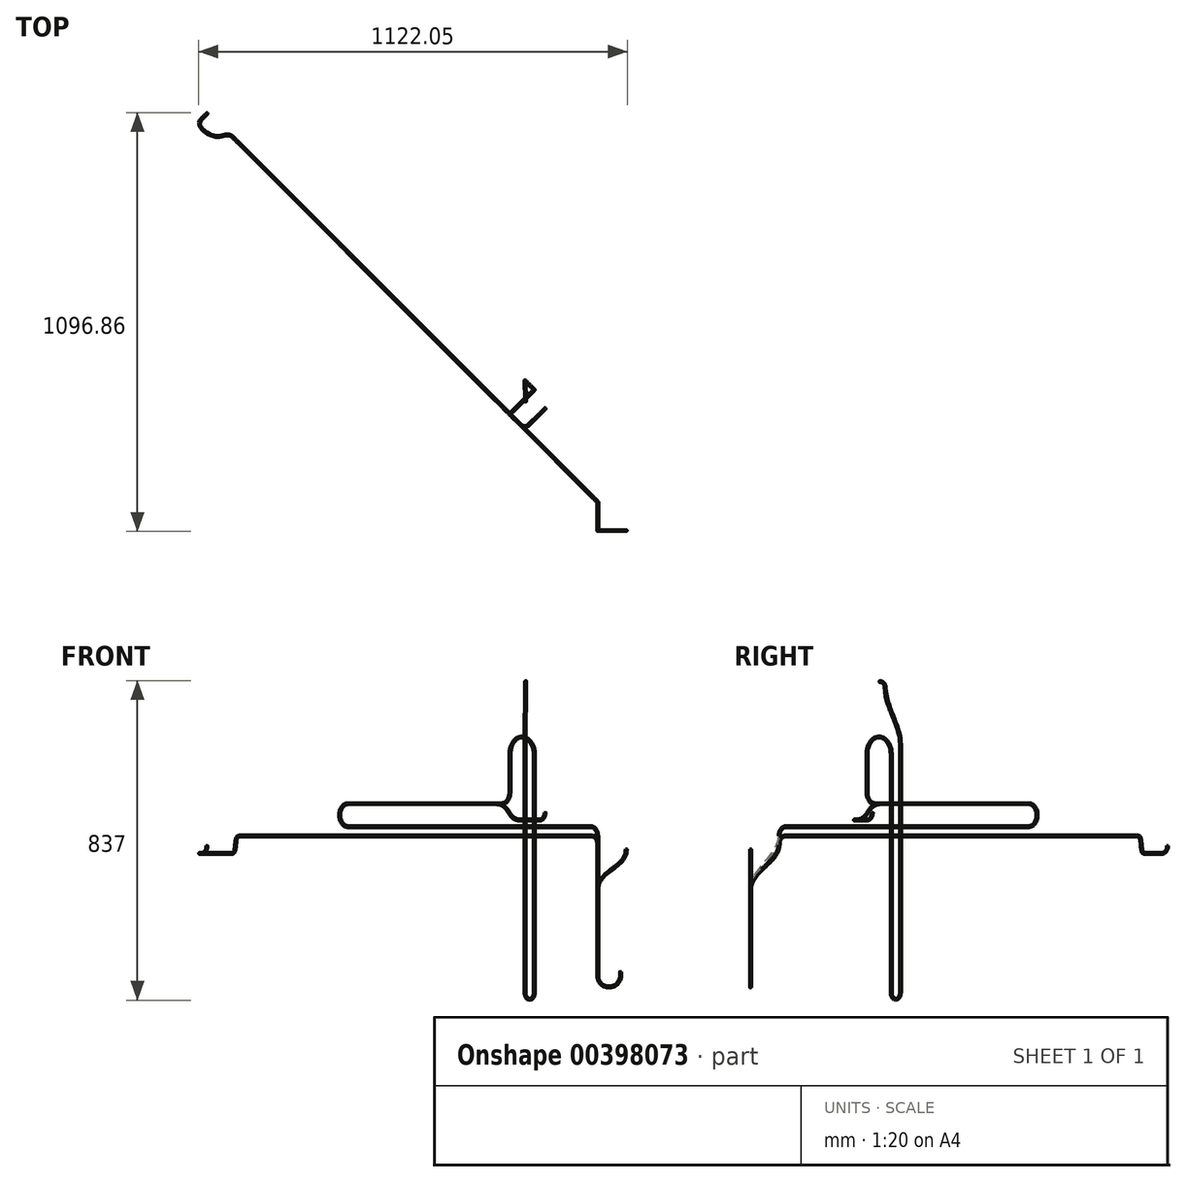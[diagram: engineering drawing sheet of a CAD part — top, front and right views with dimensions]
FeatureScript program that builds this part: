
annotation { "Feature Type Name" : "Feature", "Feature Type Description" : "" }
export const myFeature = defineFeature(function(context is Context, id is Id, definition is map)
    precondition{}
    {
        {
            var Q0;
            Q0=qCreatedBy(makeId("Top.planeOp"),FACE);
            var sketch = newSketch(context, id + "F0", { "sketchPlane" : qUnion([Q0])});
            skCircle(sketch, "E0", {"center": v(0, 0) * mm, "radius": 2.5 * mm});
            skSolve(sketch);
        }
        {
            var Q0;
            Q0=qCreatedBy(makeId("Front.planeOp"),FACE);
            var sketch = newSketch(context, id + "F1", { "sketchPlane" : qUnion([Q0])});
            skLineSegment(sketch, "E1", {"start": v(0, 0) * mm, "end": v(0, -10) * mm});
            skArc(sketch, "E2", {"start": v(-60, -10) * mm, "mid": v(-30, -40) * mm, "end": v(0, -10) * mm});
            skLineSegment(sketch, "E3", {"start": v(-60, -10) * mm, "end": v(-60, 215) * mm});
            skFitSpline(sketch, "E4", {"points": [v(-60, 215) * mm, v(-22.5, 268) * mm, v(15, 321) * mm], "startDerivative": vector(0, 150) * mm, "endDerivative": vector(0, 150) * mm});
            skLineSegment(sketch, "E5", {"start": v(15, 296) * mm, "end": v(15, 321) * mm, "construction": true});
            skLineSegment(sketch, "E6", {"start": v(-60, 240) * mm, "end": v(-60, 215) * mm, "construction": true});
            skLineSegment(sketch, "E7", {"start": v(15, 321) * mm, "end": v(-60, 215) * mm, "construction": true});
            skSolve(sketch);
        }
        {
            var Q0;
            Q0=qSketchRegion(id+"F0",true);
            var Q1;
            Q1=qConstructionFilter(qBodyType(qCreatedBy(id+"F1",EDGE),BodyType.WIRE),ConstructionObject.NO);
            sweep(context, id + "F2", {"profiles" : qUnion([Q0]), "path" : qUnion([Q1])});
        }
        {
            var Q0;
            Q0=qCreatedBy(makeId("Front.planeOp"),FACE);
            var sketch = newSketch(context, id + "F3", { "sketchPlane" : qUnion([Q0])});
            skLineSegment(sketch, "E8", {"start": v(0, 0) * mm, "end": v(0, -10) * mm});
            skArc(sketch, "E9", {"start": v(-60, -10) * mm, "mid": v(-30, -40) * mm, "end": v(0, -10) * mm});
            skLineSegment(sketch, "E10", {"start": v(-60, -10) * mm, "end": v(-60, 215) * mm});
            skSolve(sketch);
        }
        {
            var Q0;
            Q0=qCreatedBy(makeId("Right.planeOp"),FACE);
            var Q1;
            Q1=sQuery(id+"F3.wireOp",VERTEX,"E10.end");
            cPlane(context, id + "F4", {"entities" : qUnion([Q0, Q1]), "cplaneType" : CPlaneType.PLANE_POINT, "offset" : 25 * mm, "width" : 150 * mm, "height" : 150 * mm});
        }
        {
            var Q0;
            Q0=qCreatedBy(id+"F4.planeOp",FACE);
            var sketch = newSketch(context, id + "F5", { "sketchPlane" : qUnion([Q0])});
            skFitSpline(sketch, "E11", {"points": [v(0, 215) * mm, v(37.5, 275) * mm, v(75, 335) * mm], "startDerivative": vector(0, 150) * mm, "endDerivative": vector(0, 150) * mm});
            skLineSegment(sketch, "E12", {"start": v(75, 310) * mm, "end": v(75, 335) * mm, "construction": true});
            skLineSegment(sketch, "E13", {"start": v(0, 240) * mm, "end": v(0, 215) * mm, "construction": true});
            skLineSegment(sketch, "E14", {"start": v(0, 215) * mm, "end": v(75, 335) * mm, "construction": true});
            skSolve(sketch);
        }
        {
            var Q0;
            Q0=sQuery(id+"F5.wireOp",EDGE,"E12");
            cPlane(context, id + "F6", {"entities" : qUnion([Q0]), "cplaneType" : CPlaneType.LINE_ANGLE, "offset" : 25 * mm, "angle" : 135 * degree, "oppositeDirection" : true, "width" : 150 * mm, "height" : 150 * mm});
        }
        {
            var Q0;
            Q0=qCreatedBy(id+"F6.planeOp",FACE);
            var sketch = newSketch(context, id + "F7", { "sketchPlane" : qUnion([Q0])});
            skArc(sketch, "E15", {"start": v(-95.46, 335) * mm, "mid": v(-101.32, 349.14) * mm, "end": v(-115.46, 355) * mm});
            skLineSegment(sketch, "E16", {"start": v(-115.46, 355) * mm, "end": v(-1423.46, 355) * mm});
            skFitSpline(sketch, "E17", {"points": [v(-1423.46, 355) * mm, v(-1435.96, 332.5) * mm, v(-1448.46, 310) * mm], "startDerivative": vector(-60, 0) * mm, "endDerivative": vector(-60, 0) * mm});
            skLineSegment(sketch, "E18", {"start": v(-1433.46, 355) * mm, "end": v(-1423.46, 355) * mm, "construction": true});
            skLineSegment(sketch, "E19", {"start": v(-1438.46, 310) * mm, "end": v(-1448.46, 310) * mm, "construction": true});
            skLineSegment(sketch, "E20", {"start": v(-1448.46, 310) * mm, "end": v(-1423.46, 355) * mm, "construction": true});
            skSolve(sketch);
        }
        {
            var Q0;
            Q0=sQuery(id+"F7.wireOp",EDGE,"E19");
            cPlane(context, id + "F8", {"entities" : qUnion([Q0]), "cplaneType" : CPlaneType.LINE_ANGLE, "offset" : 25 * mm, "angle" : 0 * degree, "width" : 150 * mm, "height" : 150 * mm});
        }
        {
            var Q0;
            Q0=qCreatedBy(id+"F8.planeOp",FACE);
            var sketch = newSketch(context, id + "F9", { "sketchPlane" : qUnion([Q0])});
            skFitSpline(sketch, "E21", {"points": [v(-1016.72, 1031.72) * mm, v(-1061.72, 1032.72) * mm, v(-1096.72, 1077.72) * mm], "startDerivative": vector(-67.63, 67.63) * mm, "endDerivative": vector(100.16, 100.16) * mm});
            skLineSegment(sketch, "E22", {"start": v(-1114.4, 1060.04) * mm, "end": v(-1096.72, 1077.72) * mm, "construction": true});
            skLineSegment(sketch, "E23", {"start": v(-1016.72, 1031.72) * mm, "end": v(-1027.32, 1042.32) * mm, "construction": true});
            skSolve(sketch);
        }
        {
            var Q0;
            Q0=sQuery(id+"F9.wireOp",EDGE,"E22");
            cPlane(context, id + "F10", {"entities" : qUnion([Q0]), "cplaneType" : CPlaneType.LINE_ANGLE, "offset" : 25 * mm, "angle" : 90 * degree, "width" : 150 * mm, "height" : 150 * mm});
        }
        {
            var Q0;
            Q0=qCreatedBy(id+"F10.planeOp",FACE);
            var sketch = newSketch(context, id + "F11", { "sketchPlane" : qUnion([Q0])});
            skArc(sketch, "E24", {"start": v(-13.44, 310) * mm, "mid": v(0.7, 315.86) * mm, "end": v(6.56, 330) * mm});
            skSolve(sketch);
        }
        {
            var Q0;
            Q0=qSketchRegion(id+"F0",true);
            var Q1;
            Q1=qConstructionFilter(qBodyType(qCreatedBy(id+"F3",EDGE),BodyType.WIRE),ConstructionObject.NO);
            var Q2;
            Q2=qConstructionFilter(qBodyType(qCreatedBy(id+"F5",EDGE),BodyType.WIRE),ConstructionObject.NO);
            var Q3;
            Q3=qConstructionFilter(qBodyType(qCreatedBy(id+"F7",EDGE),BodyType.WIRE),ConstructionObject.NO);
            var Q4;
            Q4=qConstructionFilter(qBodyType(qCreatedBy(id+"F9",EDGE),BodyType.WIRE),ConstructionObject.NO);
            var Q5;
            Q5=qConstructionFilter(qBodyType(qCreatedBy(id+"F11",EDGE),BodyType.WIRE),ConstructionObject.NO);
            sweep(context, id + "F12", {"profiles" : qUnion([Q0]), "path" : qUnion([Q1, Q2, Q3, Q4, Q5])});
        }
        {
            var Q0;
            Q0=qCreatedBy(makeId("Front.planeOp"),FACE);
            var sketch = newSketch(context, id + "F13", { "sketchPlane" : qUnion([Q0])});
            skLineSegment(sketch, "E25", {"start": v(0, 0) * mm, "end": v(0, -10) * mm});
            skArc(sketch, "E26", {"start": v(-60, -10) * mm, "mid": v(-30, -40) * mm, "end": v(0, -10) * mm});
            skLineSegment(sketch, "E27", {"start": v(-60, -10) * mm, "end": v(-60, 215) * mm});
            skSolve(sketch);
        }
        {
            var Q0;
            Q0=qCreatedBy(makeId("Right.planeOp"),FACE);
            var Q1;
            Q1=sQuery(id+"F13.wireOp",VERTEX,"E27.end");
            cPlane(context, id + "F14", {"entities" : qUnion([Q0, Q1]), "cplaneType" : CPlaneType.PLANE_POINT, "offset" : 25 * mm, "width" : 150 * mm, "height" : 150 * mm});
        }
        {
            var Q0;
            Q0=qCreatedBy(id+"F14.planeOp",FACE);
            var sketch = newSketch(context, id + "F15", { "sketchPlane" : qUnion([Q0])});
            skFitSpline(sketch, "E28", {"points": [v(0, 215) * mm, v(37.5, 285) * mm, v(75, 355) * mm], "startDerivative": vector(0, 150) * mm, "endDerivative": vector(0, 150) * mm});
            skLineSegment(sketch, "E29", {"start": v(75, 330) * mm, "end": v(75, 355) * mm, "construction": true});
            skLineSegment(sketch, "E30", {"start": v(0, 240) * mm, "end": v(0, 215) * mm, "construction": true});
            skLineSegment(sketch, "E31", {"start": v(0, 215) * mm, "end": v(75, 355) * mm, "construction": true});
            skSolve(sketch);
        }
        {
            var Q0;
            Q0=sQuery(id+"F15.wireOp",EDGE,"E29");
            cPlane(context, id + "F16", {"entities" : qUnion([Q0]), "cplaneType" : CPlaneType.LINE_ANGLE, "offset" : 25 * mm, "angle" : 135 * degree, "oppositeDirection" : true, "width" : 150 * mm, "height" : 150 * mm});
        }
        {
            var Q0;
            Q0=qCreatedBy(id+"F16.planeOp",FACE);
            var sketch = newSketch(context, id + "F17", { "sketchPlane" : qUnion([Q0])});
            skArc(sketch, "E32", {"start": v(-95.46, 355) * mm, "mid": v(-102.78, 372.68) * mm, "end": v(-120.46, 380) * mm});
            skLineSegment(sketch, "E33", {"start": v(-120.46, 380) * mm, "end": v(-1020.46, 380) * mm});
            skArc(sketch, "E34", {"start": v(-1020.46, 440) * mm, "mid": v(-1050.46, 410) * mm, "end": v(-1020.46, 380) * mm});
            skLineSegment(sketch, "E35", {"start": v(-1020.46, 440) * mm, "end": v(-470.46, 440) * mm});
            skFitSpline(sketch, "E36", {"points": [v(-470.46, 440) * mm, v(-425.46, 418.5) * mm, v(-380.46, 397) * mm], "startDerivative": vector(150, 0) * mm, "endDerivative": vector(150, 0) * mm});
            skLineSegment(sketch, "E37", {"start": v(-445.46, 440) * mm, "end": v(-470.46, 440) * mm, "construction": true});
            skLineSegment(sketch, "E38", {"start": v(-405.46, 397) * mm, "end": v(-380.46, 397) * mm, "construction": true});
            skLineSegment(sketch, "E39", {"start": v(-380.46, 397) * mm, "end": v(-470.46, 440) * mm, "construction": true});
            skSolve(sketch);
        }
        {
            var Q0;
            Q0=qCreatedBy(makeId("Top.planeOp"),FACE);
            var Q1;
            Q1=sQuery(id+"F17.wireOp",VERTEX,"E36.end");
            cPlane(context, id + "F18", {"entities" : qUnion([Q0, Q1]), "cplaneType" : CPlaneType.PLANE_POINT, "offset" : 0 * mm, "width" : 150 * mm, "height" : 150 * mm});
        }
        {
            var Q0;
            Q0=qCreatedBy(id+"F18.planeOp",FACE);
            var sketch = newSketch(context, id + "F19", { "sketchPlane" : qUnion([Q0])});
            skArc(sketch, "E40", {"start": v(-261.53, 276.53) * mm, "mid": v(-250.92, 272.13) * mm, "end": v(-240.31, 276.53) * mm});
            skLineSegment(sketch, "E41", {"start": v(-261.53, 276.53) * mm, "end": v(-250.92, 287.13) * mm, "construction": true});
            skLineSegment(sketch, "E42", {"start": v(-240.31, 276.53) * mm, "end": v(-250.92, 287.13) * mm, "construction": true});
            skLineSegment(sketch, "E43", {"start": v(-240.31, 276.53) * mm, "end": v(-212.03, 304.8) * mm});
            skSolve(sketch);
        }
        {
            var Q0;
            Q0=sQuery(id+"F19.wireOp",EDGE,"E43");
            cPlane(context, id + "F20", {"entities" : qUnion([Q0]), "cplaneType" : CPlaneType.LINE_ANGLE, "offset" : 25 * mm, "angle" : 90 * degree, "width" : 150 * mm, "height" : 150 * mm});
        }
        {
            var Q0;
            Q0=qCreatedBy(id+"F20.planeOp",FACE);
            var sketch = newSketch(context, id + "F21", { "sketchPlane" : qUnion([Q0])});
            skArc(sketch, "E44", {"start": v(65.6, 397) * mm, "mid": v(79.75, 402.86) * mm, "end": v(85.6, 417) * mm});
            skSolve(sketch);
        }
        {
            var Q0;
            Q0=qSketchRegion(id+"F0",true);
            var Q1;
            Q1=qConstructionFilter(qBodyType(qCreatedBy(id+"F13",EDGE),BodyType.WIRE),ConstructionObject.NO);
            var Q2;
            Q2=qConstructionFilter(qBodyType(qCreatedBy(id+"F15",EDGE),BodyType.WIRE),ConstructionObject.NO);
            var Q3;
            Q3=qConstructionFilter(qBodyType(qCreatedBy(id+"F17",EDGE),BodyType.WIRE),ConstructionObject.NO);
            var Q4;
            Q4=qConstructionFilter(qBodyType(qCreatedBy(id+"F19",EDGE),BodyType.WIRE),ConstructionObject.NO);
            var Q5;
            Q5=qConstructionFilter(qBodyType(qCreatedBy(id+"F21",EDGE),BodyType.WIRE),ConstructionObject.NO);
            sweep(context, id + "F22", {"profiles" : qUnion([Q0]), "path" : qUnion([Q1, Q2, Q3, Q4, Q5])});
        }
        {
            var Q0;
            Q0=qCreatedBy(makeId("Front.planeOp"),FACE);
            var sketch = newSketch(context, id + "F23", { "sketchPlane" : qUnion([Q0])});
            skLineSegment(sketch, "E45", {"start": v(0, 0) * mm, "end": v(0, -10) * mm});
            skArc(sketch, "E46", {"start": v(-60, -10) * mm, "mid": v(-30, -40) * mm, "end": v(0, -10) * mm});
            skLineSegment(sketch, "E47", {"start": v(-60, -10) * mm, "end": v(-60, 215) * mm});
            skSolve(sketch);
        }
        {
            var Q0;
            Q0=qCreatedBy(makeId("Right.planeOp"),FACE);
            var Q1;
            Q1=sQuery(id+"F23.wireOp",VERTEX,"E47.end");
            cPlane(context, id + "F24", {"entities" : qUnion([Q0, Q1]), "cplaneType" : CPlaneType.PLANE_POINT, "offset" : 25 * mm, "width" : 150 * mm, "height" : 150 * mm});
        }
        {
            var Q0;
            Q0=qCreatedBy(id+"F24.planeOp",FACE);
            var sketch = newSketch(context, id + "F25", { "sketchPlane" : qUnion([Q0])});
            skFitSpline(sketch, "E48", {"points": [v(0, 215) * mm, v(37.5, 285) * mm, v(75, 355) * mm], "startDerivative": vector(0, 150) * mm, "endDerivative": vector(0, 150) * mm});
            skLineSegment(sketch, "E49", {"start": v(75, 330) * mm, "end": v(75, 355) * mm, "construction": true});
            skLineSegment(sketch, "E50", {"start": v(0, 240) * mm, "end": v(0, 215) * mm, "construction": true});
            skLineSegment(sketch, "E51", {"start": v(0, 215) * mm, "end": v(75, 355) * mm, "construction": true});
            skSolve(sketch);
        }
        {
            var Q0;
            Q0=sQuery(id+"F25.wireOp",EDGE,"E49");
            cPlane(context, id + "F26", {"entities" : qUnion([Q0]), "cplaneType" : CPlaneType.LINE_ANGLE, "offset" : 25 * mm, "angle" : 135 * degree, "oppositeDirection" : true, "width" : 150 * mm, "height" : 150 * mm});
        }
        {
            var Q0;
            Q0=qCreatedBy(id+"F26.planeOp",FACE);
            var sketch = newSketch(context, id + "F27", { "sketchPlane" : qUnion([Q0])});
            skArc(sketch, "E52", {"start": v(-95.46, 355) * mm, "mid": v(-102.78, 372.68) * mm, "end": v(-120.46, 380) * mm});
            skLineSegment(sketch, "E53", {"start": v(-120.46, 380) * mm, "end": v(-1020.46, 380) * mm});
            skArc(sketch, "E54", {"start": v(-1020.46, 440) * mm, "mid": v(-1050.46, 410) * mm, "end": v(-1020.46, 380) * mm});
            skLineSegment(sketch, "E55", {"start": v(-1020.46, 440) * mm, "end": v(-450.46, 440) * mm});
            skArc(sketch, "E56", {"start": v(-450.46, 440) * mm, "mid": v(-429.25, 448.79) * mm, "end": v(-420.46, 470) * mm});
            skLineSegment(sketch, "E57", {"start": v(-420.46, 470) * mm, "end": v(-420.46, 428.68) * mm, "construction": true});
            skSolve(sketch);
        }
        {
            var Q0;
            Q0=makeQuery(id+"F34.opSweep","CAP_EDGE",EDGE,{"disambiguationData":[OSD([sQuery(id+"F0.wireOp",EDGE,"E0"),sQuery(id+"F27.wireOp",VERTEX,"E56.end")])],"isStart":false});
            var Q1;
            Q1=sQuery(id+"F27.wireOp",EDGE,"E57");
            cPlane(context, id + "F28", {"entities" : qUnion([Q0, Q1]), "cplaneType" : CPlaneType.LINE_ANGLE, "offset" : 25 * mm, "angle" : 45 * degree, "width" : 150 * mm, "height" : 150 * mm});
        }
        {
            var Q0;
            Q0=qCreatedBy(id+"F28.planeOp",FACE);
            var sketch = newSketch(context, id + "F29", { "sketchPlane" : qUnion([Q0])});
            skLineSegment(sketch, "E58", {"start": v(-10.6, 470) * mm, "end": v(-10.6, 570) * mm});
            skArc(sketch, "E59", {"start": v(-10.6, 570) * mm, "mid": v(-55.6, 615) * mm, "end": v(-100.6, 570) * mm});
            skLineSegment(sketch, "E60", {"start": v(-100.6, 570) * mm, "end": v(-100.6, -55) * mm});
            skSolve(sketch);
        }
        {
            var Q0;
            Q0=sQuery(id+"F29.wireOp",EDGE,"E60");
            cPlane(context, id + "F30", {"entities" : qUnion([Q0]), "cplaneType" : CPlaneType.LINE_ANGLE, "offset" : 25 * mm, "angle" : 225 * degree, "oppositeDirection" : true, "width" : 150 * mm, "height" : 150 * mm});
        }
        {
            var Q0;
            Q0=qCreatedBy(id+"F30.planeOp",FACE);
            var sketch = newSketch(context, id + "F31", { "sketchPlane" : qUnion([Q0])});
            skLineSegment(sketch, "E61", {"start": v(454.46, -55) * mm, "end": v(454.46, 595) * mm});
            skArc(sketch, "E62", {"start": v(420.46, -55) * mm, "mid": v(437.46, -72) * mm, "end": v(454.46, -55) * mm});
            skSolve(sketch);
        }
        {
            var Q0;
            Q0=sQuery(id+"F31.wireOp",EDGE,"E61");
            cPlane(context, id + "F32", {"entities" : qUnion([Q0]), "cplaneType" : CPlaneType.LINE_ANGLE, "offset" : 25 * mm, "angle" : 2 * degree, "width" : 150 * mm, "height" : 150 * mm});
        }
        {
            var Q0;
            Q0=qCreatedBy(id+"F32.planeOp",FACE);
            var sketch = newSketch(context, id + "F33", { "sketchPlane" : qUnion([Q0])});
            skFitSpline(sketch, "E63", {"points": [v(400.98, 595) * mm, v(380.98, 670) * mm, v(360.98, 745) * mm], "startDerivative": vector(0, 150) * mm, "endDerivative": vector(0, 150) * mm});
            skLineSegment(sketch, "E64", {"start": v(400.98, 620) * mm, "end": v(400.98, 595) * mm, "construction": true});
            skLineSegment(sketch, "E65", {"start": v(360.98, 720) * mm, "end": v(360.98, 745) * mm, "construction": true});
            skLineSegment(sketch, "E66", {"start": v(360.98, 745) * mm, "end": v(400.98, 595) * mm, "construction": true});
            skArc(sketch, "E67", {"start": v(360.98, 745) * mm, "mid": v(356.6, 755.6) * mm, "end": v(345.98, 760) * mm});
            skSolve(sketch);
        }
        {
            var Q0;
            Q0=qSketchRegion(id+"F0",true);
            var Q1;
            Q1=qConstructionFilter(qBodyType(qCreatedBy(id+"F23",EDGE),BodyType.WIRE),ConstructionObject.NO);
            var Q2;
            Q2=qConstructionFilter(qBodyType(qCreatedBy(id+"F25",EDGE),BodyType.WIRE),ConstructionObject.NO);
            var Q3;
            Q3=qConstructionFilter(qBodyType(qCreatedBy(id+"F27",EDGE),BodyType.WIRE),ConstructionObject.NO);
            var Q4;
            Q4=qConstructionFilter(qBodyType(qCreatedBy(id+"F29",EDGE),BodyType.WIRE),ConstructionObject.NO);
            var Q5;
            Q5=qConstructionFilter(qBodyType(qCreatedBy(id+"F31",EDGE),BodyType.WIRE),ConstructionObject.NO);
            var Q6;
            Q6=qConstructionFilter(qBodyType(qCreatedBy(id+"F33",EDGE),BodyType.WIRE),ConstructionObject.NO);
            sweep(context, id + "F34", {"profiles" : qUnion([Q0]), "path" : qUnion([Q1, Q2, Q3, Q4, Q5, Q6])});
        }
    });
